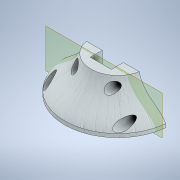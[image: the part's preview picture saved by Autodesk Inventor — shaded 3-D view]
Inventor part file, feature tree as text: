
AUTODESK INVENTOR PART (.ipt)
format: ipt  version: 2021 (Build 250183000, 183)  size: 280,064 bytes
history: native  units: mm
features: sketch x6, extrude x5, plane x2, revolve x1, split x1
ambient origin geometry x8: Origin, YZ Plane, XZ Plane, XY Plane, X Axis, Y Axis, Z Axis, Center Point
bodies: Solid1 (feature_tree)
feature tree (15):
  revolve  "Revolution1"  [1 undecoded]
  extrude  "Extrusion1"  Depth=5.0mm
  extrude  "Extrusion2"  Depth=30.0mm
  extrude  "Extrusion3"  Depth=24.0mm
  plane  "Work Plane1"
  split  "Split1"
  extrude  "Extrusion4"  Depth=35.0mm TaperAngle=0.0deg
  plane  "Work Plane2"
  extrude  "Extrusion5"  Depth=50.0mm TaperAngle=0.0deg
  sketch  "Sketch1"  dims[d0=75.0mm d1=50.0mm]
  sketch  "Sketch2"  dims[d2=38.0mm d3=5.0mm]
  sketch  "Sketch3"  dims[d4=90.0deg d5=30.0mm]
  sketch  "Sketch4"  dims[d6=48.0mm d7=24.0mm]
  sketch  "Sketch6"  dims[d8=15.0mm d9=35.0mm d10=0.0mm]
  sketch  "Sketch7"  dims[d11=17.0mm d12=8.0mm d13=0.0mm d14=5.2mm d15=5.2mm d16=12.0mm d17=12.0mm d18=22.0mm d19=12.0mm d20=52.0mm d21=52.0mm d22=0.0mm d23=0.0mm d24=0.0mm d25=21.0mm d26=2.5mm d27=0.0mm d28=-12.5mm d29=12.5mm d30=12.5mm d31=12.5mm d32=12.5mm d33=50.0mm d34=0.0mm]
note: 1 required parameter value undecoded (feature->parameter linkage not recoverable at this tier; creation-order binding heuristic only, values carry confidence <= 0.55)
